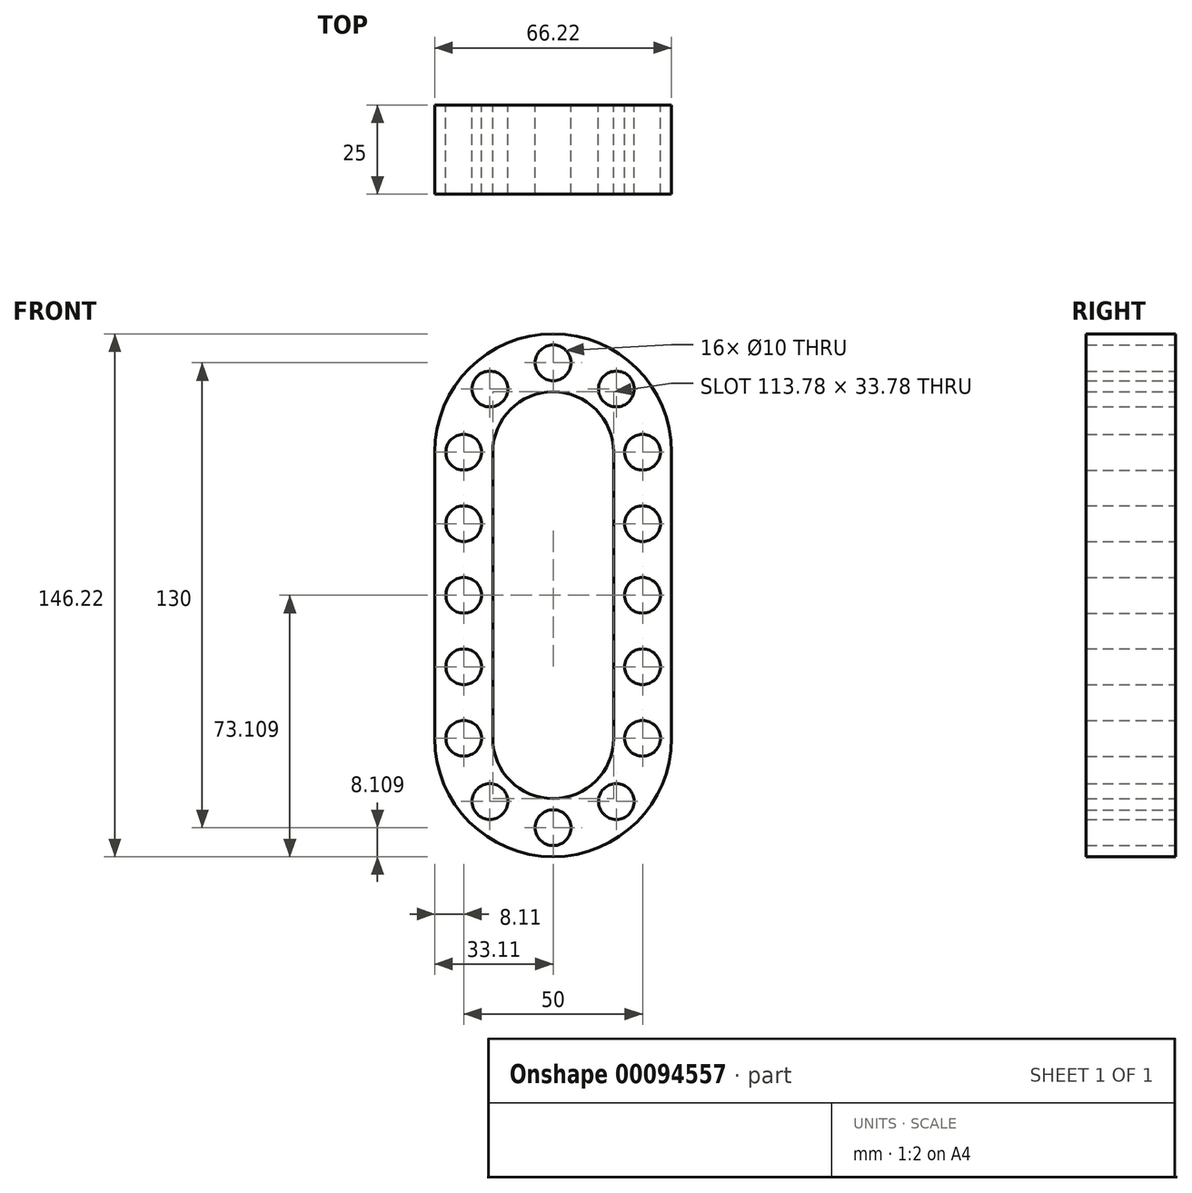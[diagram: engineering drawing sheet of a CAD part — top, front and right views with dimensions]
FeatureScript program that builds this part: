
annotation { "Feature Type Name" : "Feature", "Feature Type Description" : "" }
export const myFeature = defineFeature(function(context is Context, id is Id, definition is map)
    precondition{}
    {
        {
            var Q0;
            Q0=qCreatedBy(makeId("Front.planeOp"),FACE);
            var sketch = newSketch(context, id + "F0", { "sketchPlane" : qUnion([Q0])});
            skPoint(sketch, "E0", {"position": v(-25, 44.84) * mm});
            skLineSegment(sketch, "E1", {"start": v(-25, 44.84) * mm, "end": v(-25, 0) * mm, "construction": true});
            skArc(sketch, "E2", {"start": v(0, 69.84) * mm, "mid": v(-17.68, 62.52) * mm, "end": v(-25, 44.84) * mm, "construction": true});
            skArc(sketch, "E3.0.endCap", {"start": v(-16.89, 44.84) * mm, "mid": v(-25, 36.73) * mm, "end": v(-33.11, 44.84) * mm, "construction": true});
            skArc(sketch, "E3.0.left", {"start": v(0, 61.73) * mm, "mid": v(-11.94, 56.78) * mm, "end": v(-16.89, 44.84) * mm});
            skArc(sketch, "E3.0.right", {"start": v(0, 77.95) * mm, "mid": v(-23.41, 68.25) * mm, "end": v(-33.11, 44.84) * mm});
            skArc(sketch, "E3.1.startCap", {"start": v(-33.11, 44.84) * mm, "mid": v(-25, 52.95) * mm, "end": v(-16.89, 44.84) * mm, "construction": true});
            skLineSegment(sketch, "E3.1.left", {"start": v(-16.89, 44.84) * mm, "end": v(-16.89, 4.84) * mm});
            skLineSegment(sketch, "E3.1.right", {"start": v(-33.11, 44.84) * mm, "end": v(-33.11, 4.84) * mm});
            skCircle(sketch, "E4", {"center": v(-25, 44.84) * mm, "radius": 5 * mm});
            skCircle(sketch, "E5.0.1.0", {"center": v(-25, 24.84) * mm, "radius": 5 * mm});
            skCircle(sketch, "E5.0.2.0", {"center": v(-25, 4.84) * mm, "radius": 5 * mm});
            skLineSegment(sketch, "E5.direction1", {"start": v(-25, 44.84) * mm, "end": v(0, 44.84) * mm, "construction": true});
            skLineSegment(sketch, "E5.direction2", {"start": v(-25, 44.84) * mm, "end": v(-25, 24.84) * mm, "construction": true});
            skCircle(sketch, "E6", {"center": v(-17.68, 62.52) * mm, "radius": 5 * mm});
            skCircle(sketch, "E7", {"center": v(0, 69.84) * mm, "radius": 5 * mm});
            skPoint(sketch, "E8.MirrorP", {"position": v(25, 44.84) * mm});
            skArc(sketch, "E9.MirrorCS", {"start": v(16.89, 44.84) * mm, "mid": v(25, 36.73) * mm, "end": v(33.11, 44.84) * mm, "construction": true});
            skLineSegment(sketch, "E10.MirrorCS", {"start": v(25, 44.84) * mm, "end": v(25, 24.84) * mm, "construction": true});
            skLineSegment(sketch, "E11.MirrorCS", {"start": v(33.11, 44.84) * mm, "end": v(33.11, 4.84) * mm});
            skCircle(sketch, "E12.MirrorC", {"center": v(25, 44.84) * mm, "radius": 5 * mm});
            skCircle(sketch, "E13.MirrorC", {"center": v(17.68, 62.52) * mm, "radius": 5 * mm});
            skCircle(sketch, "E14.MirrorC", {"center": v(25, 24.84) * mm, "radius": 5 * mm});
            skArc(sketch, "E15.MirrorCS", {"start": v(33.11, 44.84) * mm, "mid": v(25, 52.95) * mm, "end": v(16.89, 44.84) * mm, "construction": true});
            skLineSegment(sketch, "E16.MirrorCS", {"start": v(16.89, 44.84) * mm, "end": v(16.89, 4.84) * mm});
            skArc(sketch, "E17.MirrorCS", {"start": v(0, 61.73) * mm, "mid": v(11.94, 56.78) * mm, "end": v(16.89, 44.84) * mm});
            skArc(sketch, "E18.MirrorCS", {"start": v(0, 77.95) * mm, "mid": v(23.41, 68.25) * mm, "end": v(33.11, 44.84) * mm});
            skArc(sketch, "E19.MirrorCS", {"start": v(0, 69.84) * mm, "mid": v(17.68, 62.52) * mm, "end": v(25, 44.84) * mm, "construction": true});
            skCircle(sketch, "E20.MirrorC", {"center": v(25, 4.84) * mm, "radius": 5 * mm});
            skArc(sketch, "E21.MirrorCS", {"start": v(0, -60.16) * mm, "mid": v(17.68, -52.84) * mm, "end": v(25, -35.16) * mm, "construction": true});
            skLineSegment(sketch, "E22.MirrorCS", {"start": v(16.89, -35.16) * mm, "end": v(16.89, 4.84) * mm});
            skPoint(sketch, "E23.MirrorP", {"position": v(-25, -35.16) * mm});
            skCircle(sketch, "E24.MirrorC", {"center": v(25, -35.16) * mm, "radius": 5 * mm});
            skArc(sketch, "E25.MirrorCS", {"start": v(-16.89, -35.16) * mm, "mid": v(-25, -27.05) * mm, "end": v(-33.11, -35.16) * mm, "construction": true});
            skLineSegment(sketch, "E26.MirrorCS", {"start": v(-33.11, -35.16) * mm, "end": v(-33.11, 4.84) * mm});
            skCircle(sketch, "E27.MirrorC", {"center": v(17.68, -52.84) * mm, "radius": 5 * mm});
            skLineSegment(sketch, "E28.MirrorCS", {"start": v(-16.89, -35.16) * mm, "end": v(-16.89, 4.84) * mm});
            skArc(sketch, "E29.MirrorCS", {"start": v(0, -52.05) * mm, "mid": v(11.94, -47.1) * mm, "end": v(16.89, -35.16) * mm});
            skArc(sketch, "E30.MirrorCS", {"start": v(-33.11, -35.16) * mm, "mid": v(-25, -43.27) * mm, "end": v(-16.89, -35.16) * mm, "construction": true});
            skLineSegment(sketch, "E31.MirrorCS", {"start": v(-25, -35.16) * mm, "end": v(-25, -15.16) * mm, "construction": true});
            skCircle(sketch, "E32.MirrorC", {"center": v(0, -60.16) * mm, "radius": 5 * mm});
            skLineSegment(sketch, "E33.MirrorCS", {"start": v(33.11, -35.16) * mm, "end": v(33.11, 4.84) * mm});
            skArc(sketch, "E34.MirrorCS", {"start": v(0, -52.05) * mm, "mid": v(-11.94, -47.1) * mm, "end": v(-16.89, -35.16) * mm});
            skCircle(sketch, "E35.MirrorC", {"center": v(-25, -15.16) * mm, "radius": 5 * mm});
            skArc(sketch, "E36.MirrorCS", {"start": v(16.89, -35.16) * mm, "mid": v(25, -27.05) * mm, "end": v(33.11, -35.16) * mm, "construction": true});
            skCircle(sketch, "E37.MirrorC", {"center": v(-17.68, -52.84) * mm, "radius": 5 * mm});
            skArc(sketch, "E38.MirrorCS", {"start": v(33.11, -35.16) * mm, "mid": v(25, -43.27) * mm, "end": v(16.89, -35.16) * mm, "construction": true});
            skArc(sketch, "E39.MirrorCS", {"start": v(0, -68.27) * mm, "mid": v(23.41, -58.57) * mm, "end": v(33.11, -35.16) * mm});
            skLineSegment(sketch, "E40.MirrorCS", {"start": v(25, -35.16) * mm, "end": v(25, -15.16) * mm, "construction": true});
            skCircle(sketch, "E41.MirrorC", {"center": v(25, -15.16) * mm, "radius": 5 * mm});
            skLineSegment(sketch, "E42.MirrorCS", {"start": v(-25, -35.16) * mm, "end": v(-25, 9.68) * mm, "construction": true});
            skArc(sketch, "E43.MirrorCS", {"start": v(0, -60.16) * mm, "mid": v(-17.68, -52.84) * mm, "end": v(-25, -35.16) * mm, "construction": true});
            skCircle(sketch, "E44.MirrorC", {"center": v(-25, -35.16) * mm, "radius": 5 * mm});
            skLineSegment(sketch, "E45.MirrorCS", {"start": v(-25, -35.16) * mm, "end": v(0, -35.16) * mm, "construction": true});
            skArc(sketch, "E46.MirrorCS", {"start": v(0, -68.27) * mm, "mid": v(-23.41, -58.57) * mm, "end": v(-33.11, -35.16) * mm});
            skSolve(sketch);
        }
        {
            var Q0;
            Q0=makeQuery(id+"F0.imprint","IMPRINT",FACE,{"disambiguationData":[TD([[makeQuery(id+"F0.imprint","IMPRINT",EDGE,{"derivedFrom":sQuery(id+"F0.wireOp",EDGE,"E3.0.left")}),-1.0]])]});
            extrude(context, id + "F1", {"entities" : qUnion([Q0]), "depth" : 25 * mm});
        }
        {
            var Q0;
            Q0 = qSketchRegion(id + "F0", true);
            extrude(context, id + "F2", {"entities" : qUnion([Q0]), "operationType" : NewBodyOperationType.ADD, "depth" : 25 * mm});
        }
    });
